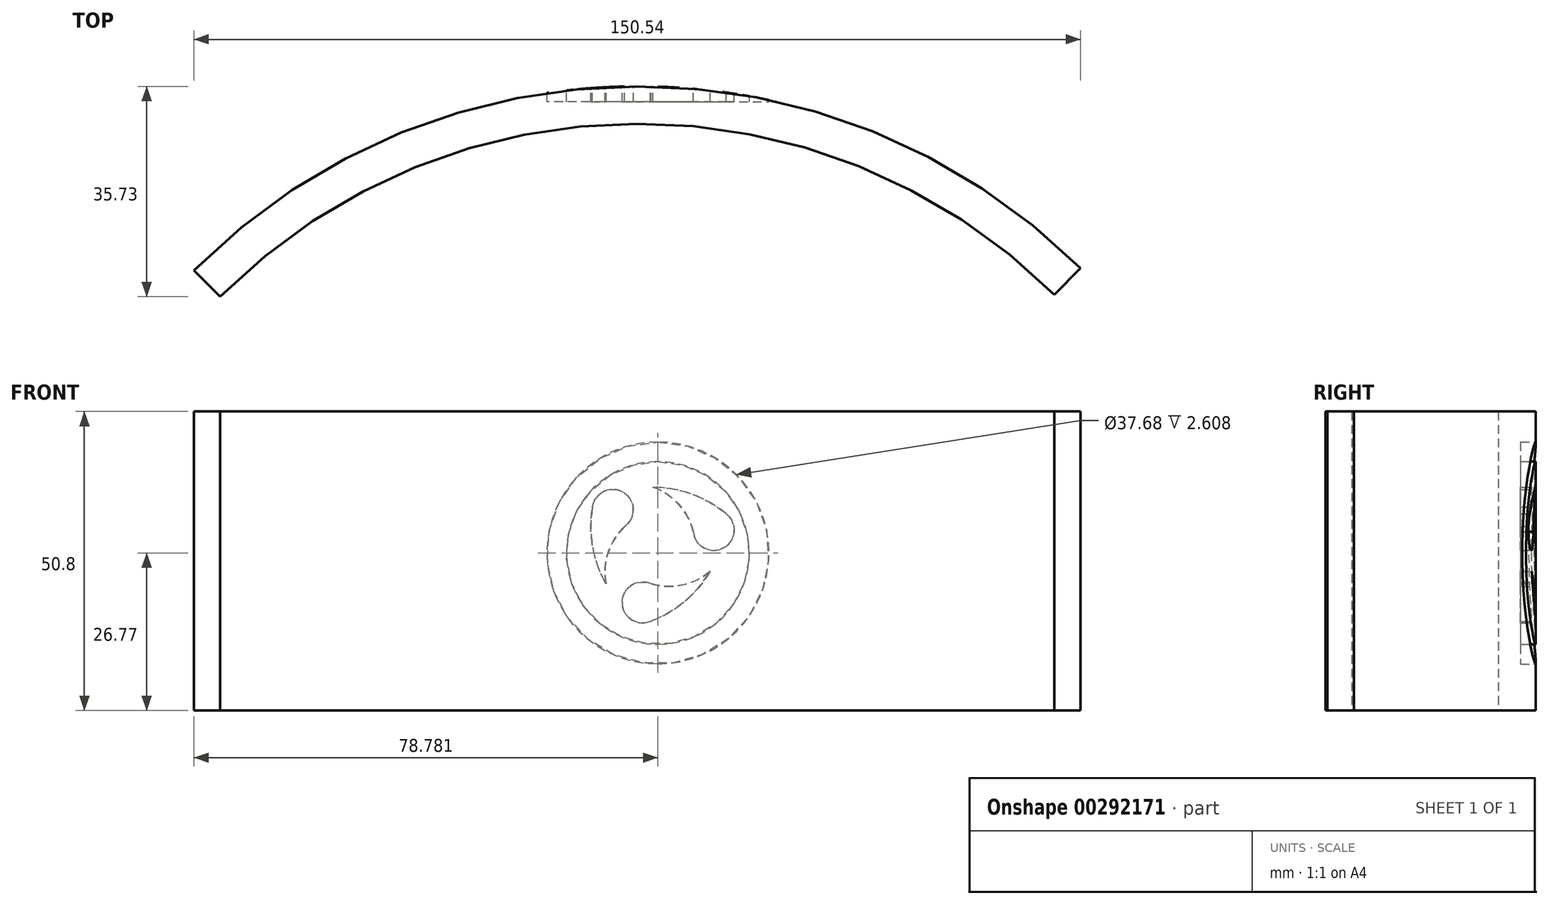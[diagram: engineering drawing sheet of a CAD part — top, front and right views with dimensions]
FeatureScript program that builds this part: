
annotation { "Feature Type Name" : "Feature", "Feature Type Description" : "" }
export const myFeature = defineFeature(function(context is Context, id is Id, definition is map)
    precondition{}
    {
        {
            var Q0;
            Q0=qCreatedBy(makeId("Top.planeOp"),FACE);
            var sketch = newSketch(context, id + "F0", { "sketchPlane" : qUnion([Q0])});
            skArc(sketch, "E0", {"start": v(76.15, -13.03) * mm, "mid": v(0.81, 17.85) * mm, "end": v(-74.39, -13.39) * mm});
            skArc(sketch, "E1.0", {"start": v(71.68, -17.55) * mm, "mid": v(0.82, 11.5) * mm, "end": v(-69.9, -17.88) * mm});
            skLineSegment(sketch, "E2", {"start": v(-74.39, -13.39) * mm, "end": v(-69.9, -17.88) * mm});
            skLineSegment(sketch, "E3", {"start": v(76.15, -13.03) * mm, "end": v(71.68, -17.55) * mm});
            skSolve(sketch);
        }
        {
            var Q0;
            Q0=makeQuery(id+"F0.imprint","IMPRINT",FACE,{"disambiguationData":[TD([[makeQuery(id+"F0.imprint","IMPRINT",EDGE,{"derivedFrom":sQuery(id+"F0.wireOp",EDGE,"E0")}),1.0]])]});
            extrude(context, id + "F1", {"entities" : qUnion([Q0]), "depth" : 50.8 * mm});
        }
        {
            var Q0;
            Q0=qCreatedBy(makeId("Front.planeOp"),FACE);
            cPlane(context, id + "F2", {"entities" : qUnion([Q0]), "cplaneType" : CPlaneType.OFFSET, "offset" : 20.32 * mm, "oppositeDirection" : true, "width" : 152.4 * mm, "height" : 152.4 * mm});
        }
        {
            var Q0;
            Q0=qCreatedBy(id+"F2.planeOp",FACE);
            var sketch = newSketch(context, id + "F3", { "sketchPlane" : qUnion([Q0])});
            skCircle(sketch, "E4", {"center": v(4.4, 26.77) * mm, "radius": 15.52 * mm});
            skCircle(sketch, "E5", {"center": v(4.4, 26.77) * mm, "radius": 18.84 * mm});
            skArc(sketch, "E6", {"start": v(10.4, 30.36) * mm, "mid": v(15.53, 27.62) * mm, "end": v(16.03, 33.4) * mm});
            skArc(sketch, "E7", {"start": v(16.03, 33.4) * mm, "mid": v(10.18, 36.76) * mm, "end": v(3.56, 37.96) * mm});
            skArc(sketch, "E8", {"start": v(10.4, 30.36) * mm, "mid": v(7.94, 35.03) * mm, "end": v(3.56, 37.96) * mm});
            skArc(sketch, "E9.1.0", {"start": v(-1.26, 31.26) * mm, "mid": v(-1.44, 37.06) * mm, "end": v(-6.7, 34.6) * mm});
            skArc(sketch, "E9.1.1", {"start": v(-1.26, 31.26) * mm, "mid": v(-4.06, 26.79) * mm, "end": v(-4.42, 21.52) * mm});
            skArc(sketch, "E9.1.2", {"start": v(-6.7, 34.6) * mm, "mid": v(-6.69, 27.86) * mm, "end": v(-4.42, 21.52) * mm});
            skArc(sketch, "E9.2.0", {"start": v(3.26, 21.52) * mm, "mid": v(-1.68, 18.46) * mm, "end": v(3.08, 15.14) * mm});
            skArc(sketch, "E9.2.1", {"start": v(3.26, 21.52) * mm, "mid": v(8.53, 21.33) * mm, "end": v(13.26, 23.66) * mm});
            skArc(sketch, "E9.2.2", {"start": v(3.08, 15.14) * mm, "mid": v(8.9, 18.52) * mm, "end": v(13.26, 23.66) * mm});
            skPoint(sketch, "E9.center", {"position": v(0, 0) * mm});
            skSolve(sketch);
        }
        {
            var Q0;
            Q0 = qSketchRegion(id + "F3", true);
            var Q1;
            Q1=makeQuery(id+"F3.imprint","IMPRINT",FACE,{"disambiguationData":[TD([[makeQuery(id+"F3.imprint","IMPRINT",EDGE,{"derivedFrom":sQuery(id+"F3.wireOp",EDGE,"E9.1.0")}),1.0]])]});
            var Q2;
            Q2=makeQuery(id+"F3.imprint","IMPRINT",FACE,{"disambiguationData":[TD([[makeQuery(id+"F3.imprint","IMPRINT",EDGE,{"derivedFrom":sQuery(id+"F3.wireOp",EDGE,"E6")}),1.0]])]});
            var Q3;
            Q3=makeQuery(id+"F3.imprint","IMPRINT",FACE,{"disambiguationData":[TD([[makeQuery(id+"F3.imprint","IMPRINT",EDGE,{"derivedFrom":sQuery(id+"F3.wireOp",EDGE,"E9.2.0")}),1.0]])]});
            extrude(context, id + "F4", {"entities" : qUnion([Q0, Q1, Q2, Q3]), "operationType" : NewBodyOperationType.REMOVE, "depth" : 5.08 * mm});
        }
    });
